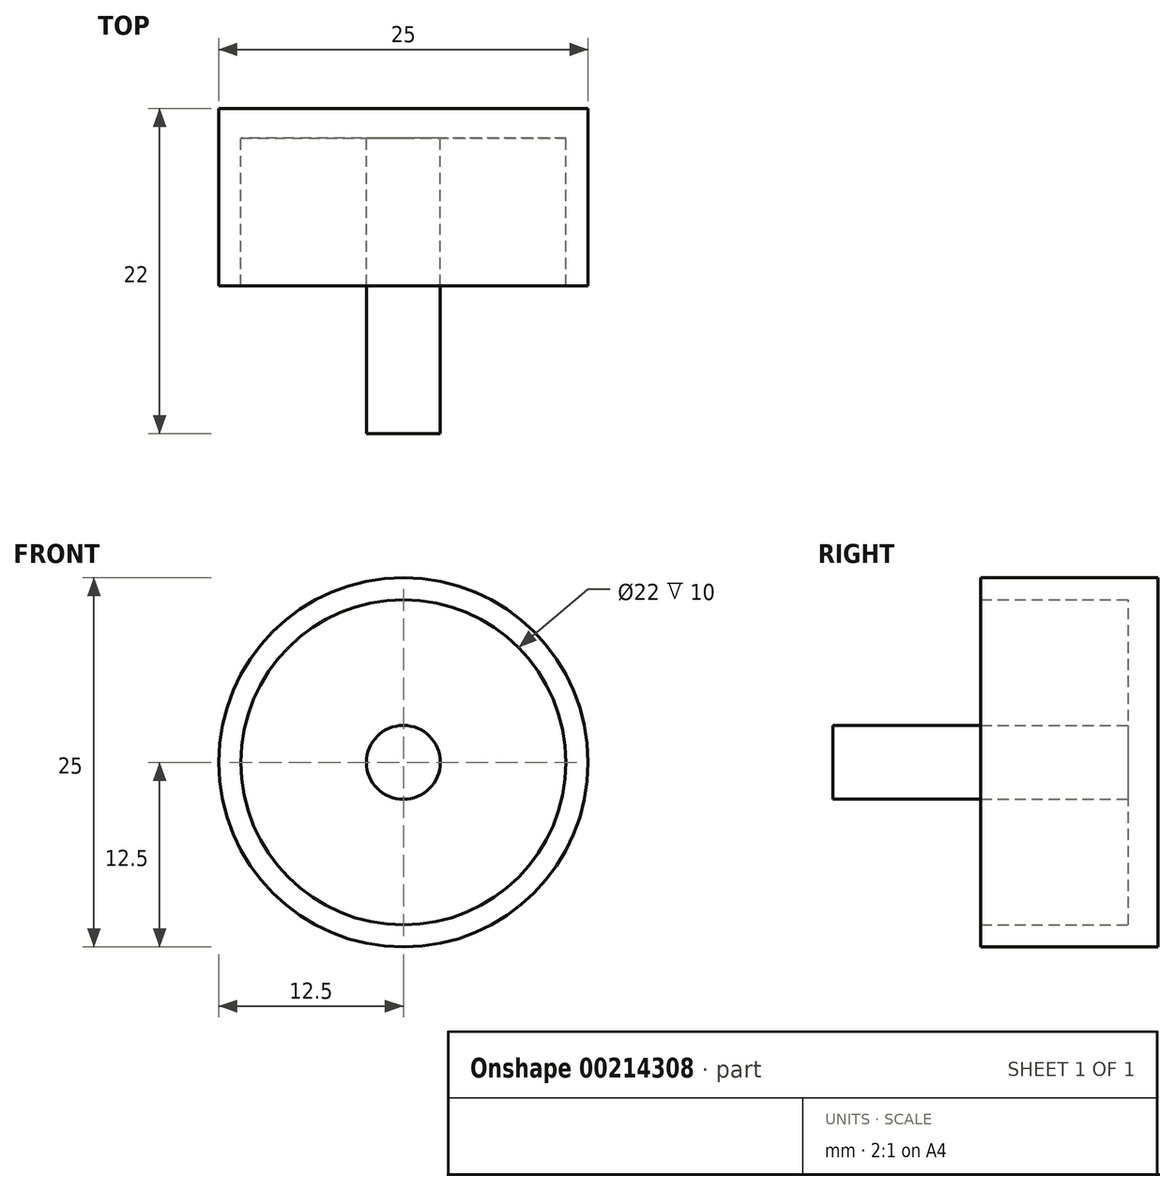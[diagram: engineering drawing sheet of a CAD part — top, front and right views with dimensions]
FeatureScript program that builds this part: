
annotation { "Feature Type Name" : "Feature", "Feature Type Description" : "" }
export const myFeature = defineFeature(function(context is Context, id is Id, definition is map)
    precondition{}
    {
        {
            var Q0;
            Q0=qCreatedBy(makeId("Front.planeOp"),FACE);
            var sketch = newSketch(context, id + "F0", { "sketchPlane" : qUnion([Q0])});
            skCircle(sketch, "E0", {"center": v(0, 0) * mm, "radius": 12.5 * mm});
            skSolve(sketch);
        }
        {
            var Q0;
            Q0 = qSketchRegion(id + "F0", true);
            extrude(context, id + "F1", {"entities" : qUnion([Q0]), "depth" : 2 * mm});
        }
        {
            var Q0;
            Q0=makeQuery(id+"F1.opExtrude","CAP_FACE",FACE,{"disambiguationData":[OSD([sQuery(id+"F0.wireOp",EDGE,"E0")])],"isStart":false});
            var sketch = newSketch(context, id + "F2", { "sketchPlane" : qUnion([Q0])});
            skCircle(sketch, "E1", {"center": v(0, 0) * mm, "radius": 12.5 * mm});
            skCircle(sketch, "E2", {"center": v(0, 0) * mm, "radius": 11 * mm});
            skSolve(sketch);
        }
        {
            var Q0;
            Q0 = qSketchRegion(id + "F2", true);
            extrude(context, id + "F3", {"entities" : qUnion([Q0]), "operationType" : NewBodyOperationType.ADD, "depth" : 10 * mm});
        }
        {
            var Q0;
            Q0=makeQuery(id+"F1.opExtrude","CAP_FACE",FACE,{"disambiguationData":[OSD([sQuery(id+"F0.wireOp",EDGE,"E0")])],"isStart":false});
            var sketch = newSketch(context, id + "F4", { "sketchPlane" : qUnion([Q0])});
            skCircle(sketch, "E3", {"center": v(0, 0) * mm, "radius": 2.5 * mm});
            skSolve(sketch);
        }
        {
            var Q0;
            Q0 = qSketchRegion(id + "F4", true);
            extrude(context, id + "F5", {"entities" : qUnion([Q0]), "operationType" : NewBodyOperationType.ADD, "depth" : 20 * mm});
        }
    });
